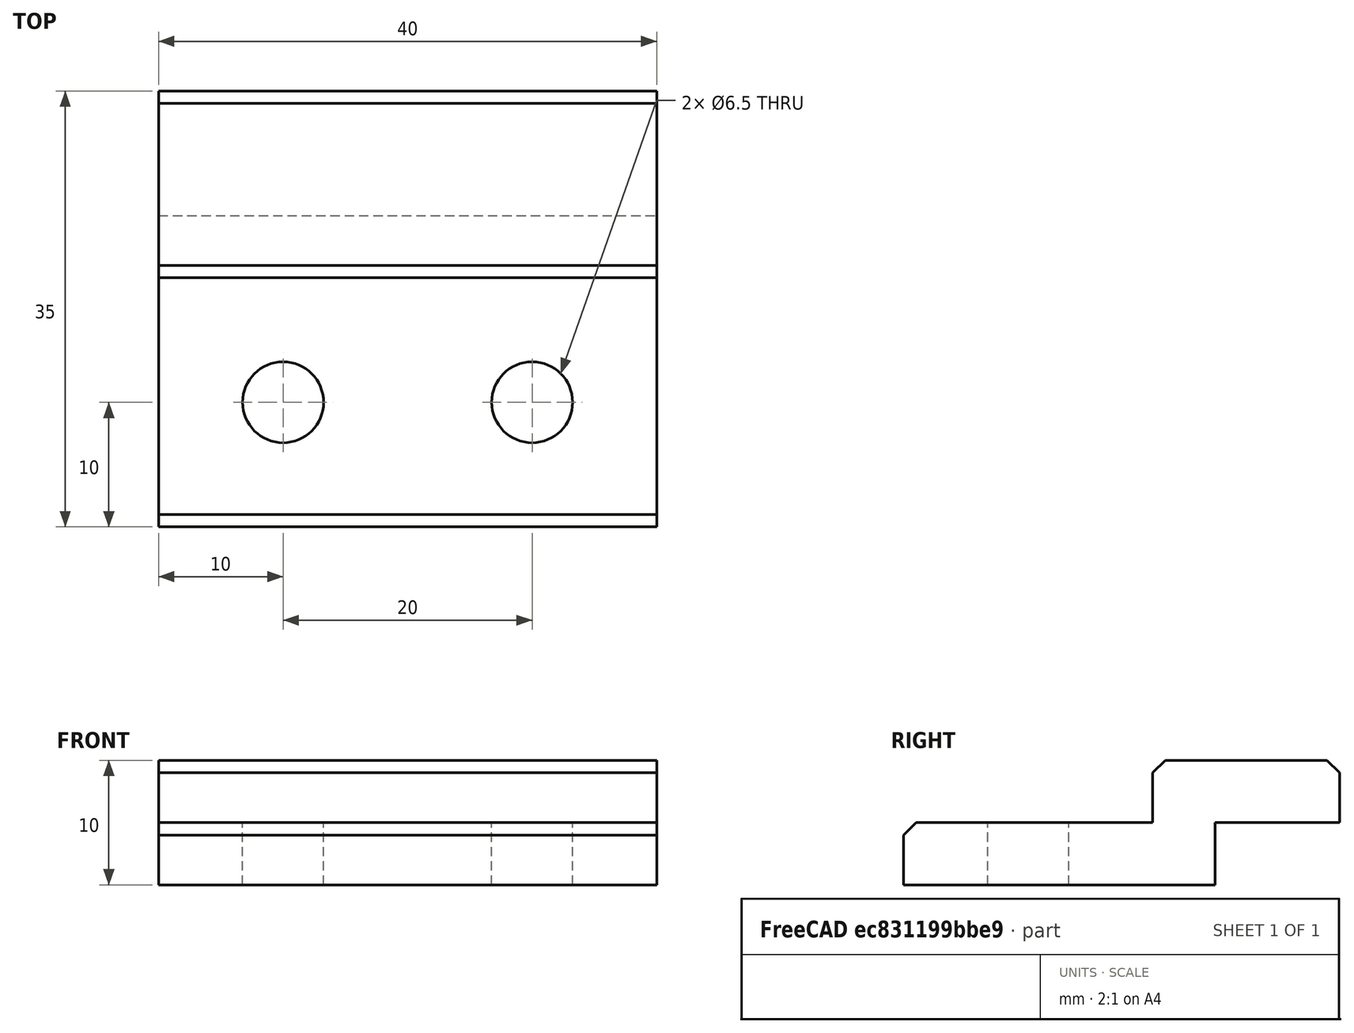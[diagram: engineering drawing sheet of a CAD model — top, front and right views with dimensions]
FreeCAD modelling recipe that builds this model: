
FCSTD DOCUMENT  (FreeCAD 0.14R3703 (Git))
Label: guia_cubeta_frontal_izq
License: CC-BY 3.0
LicenseURL: http://creativecommons.org/licenses/by/3.0/
objects: Part::Chamfer×3, Part::Box×2, Part::Cylinder×2, Part::Cut×2, Part::Fuse×1, Part::Feature×1
note: 11 computed .brp shape members not serialized (recipe doc carries the construction recipe); baked Part::Feature solids carry a one-line shape summary decoded from their .brp

FEATURE [Part::Box] Box  label="Cubo"
  Height = 5
  Length = 40
  Width = 25
FEATURE [Part::Box] Box001  label="Cubo001"
  Height = 5
  Length = 40
  Placement = pos=(0,20,5) rot=(0,0,1;0rad)
  Width = 15
FEATURE [Part::Chamfer] Chamfer
  Base = -> Box
  Edges = 1 edges r=1: [Edge10]
FEATURE [Part::Chamfer] Chamfer001
  Base = -> Box001
  Edges = 1 edges r=1: [Edge10]
FEATURE [Part::Chamfer] Chamfer002
  Base = -> Chamfer001
  Edges = 1 edges r=1: [Edge13]
FEATURE [Part::Fuse] Fusion
  Base = -> Chamfer
  Tool = -> Chamfer002
FEATURE [Part::Cylinder] Cylinder  label="Cilindro"
  Angle = 360
  Height = 10
  Placement = pos=(10,10,0) rot=(0,0,1;0rad)
  Radius = 3.25
FEATURE [Part::Cut] Cut
  Base = -> Fusion
  Tool = -> Cylinder
FEATURE [Part::Cylinder] Cylinder001  label="Cilindro001"
  Angle = 360
  Height = 10
  Placement = pos=(30,10,0) rot=(0,0,1;0rad)
  Radius = 3.25
FEATURE [Part::Cut] Cut001
  Base = -> Cut
  Tool = -> Cylinder001
FEATURE [Part::Feature] Cut001001  label="guia_cubeta_ant_izq"
  shape: bbox 40 x 35 x 10 mm, 15 faces (baked)
